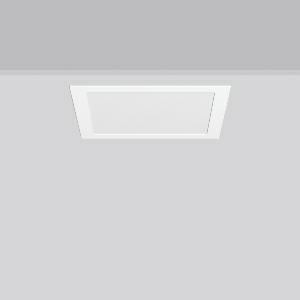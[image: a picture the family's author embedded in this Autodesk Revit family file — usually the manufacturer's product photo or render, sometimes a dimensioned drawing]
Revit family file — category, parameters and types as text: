
# Revit family: toledo_flat_square_e_672239_002_1_a966
name_source: partatom
category: Lighting Fixtures
units: mm (PartAtom-declared; Revit-internal decimal feet)

## family parameters
Cut with Voids When Loaded = No
Host = Face
Light Source = No
Part Type = Normal
Room Calculation Point = No
Round Connector Dimension = Use Diameter
Shared = No

## types (1)
- TOLEDO FLAT square E (1 x LED Modul 840, 2200 lm, 4000)
    Apparent Load = 25 VA
    CIE Flux Codes = 49 80 96 100 100
    Color Rendering = 80
    Color Temperature = 4000
    Default Elevation = 1800 mm
    Description = Series: TOLEDO FLAT square
Square recessed downlight. For escape route illumination. Housing: die-cast aluminium, powder-coated. Lightguide and diffuser made of non-yellowing plastic (PMMA). Diffuser opal matt plastic. Ceiling installation with spring system. Including separate LED converter with connecting cable 250 mm. Self-contained system with automatic self-test. External driver with simple plug-in locking system. 
Colour: white
Length: 300 mm
Width: 300 mm
Height: 3 mm
Cut-out length: 280 mm
Cut-out width: 280 mm
Recess height: 90 mm
Luminaire: recess height: 60-80 mm
Weight: 2.23 kg
Operating mode: maintained power mode
Duration time: 3 h
Lamp: LED
Socket: without socket
Colour temperature: 4000K
Colour rendering index (CRI): 80
System power: 25 W
Rated luminous flux: 2200 lm
Luminous flux, emergency: 430 lm
System power, emergency: -
Control gear: Regulated power supply
Protection class: I
Type of protection: IP 54
    Height = 0 mm  [stored 0 ft]
    Lamp = 1 x LED Modul 840
    Lamp Light Flux = 2200 lm
    Lamp count = 1
    Length = 300 mm
    Lifetime = 50000 h
    Luminous efficacy = 88 lm/W
    Manufacturer = RZB
    ModVariant = No
    Model = 672239.002.1
    Mounting Place = Ceiling
    Mounting Type = Recessed
    Number of Poles = 1
    OnlyDefault = Yes
    Power Factor = 1
    Product Name = TOLEDO FLAT square E
    Product group = Recessed downlights
    ProductGroupID = 402
    Protection Class = Protection class I
    Protection Degree = IP 40
    RLX_Detail_Level = 1
    RLX_Emergency_Light_Flux = 430 lm
    RLX_Emergency_Type = 3
    RLX_Emergency_Type_DB = Yes
    RlxData = <blob elided: 13213 chars, md5=ef95ffbb>
    Socket = socket
    Standby Power = 0 W
    System Light Flux = 2200 lm
    System Power = 25 W
    Type Comments = Product without accessories
    Type Image = 901488.002.jpg
    URL = http://relux.com
    VarID = ---
    Voltage = 0 V
    Weight = 0.00 kg
    Width = 300 mm

note: [stored X ft] marks values corroborated as IEEE doubles in the binary element streams (Revit-internal decimal feet)

## geometry (parser evidence)
native form markers: Sweep x9
no freeform markers — native parametric forms only
